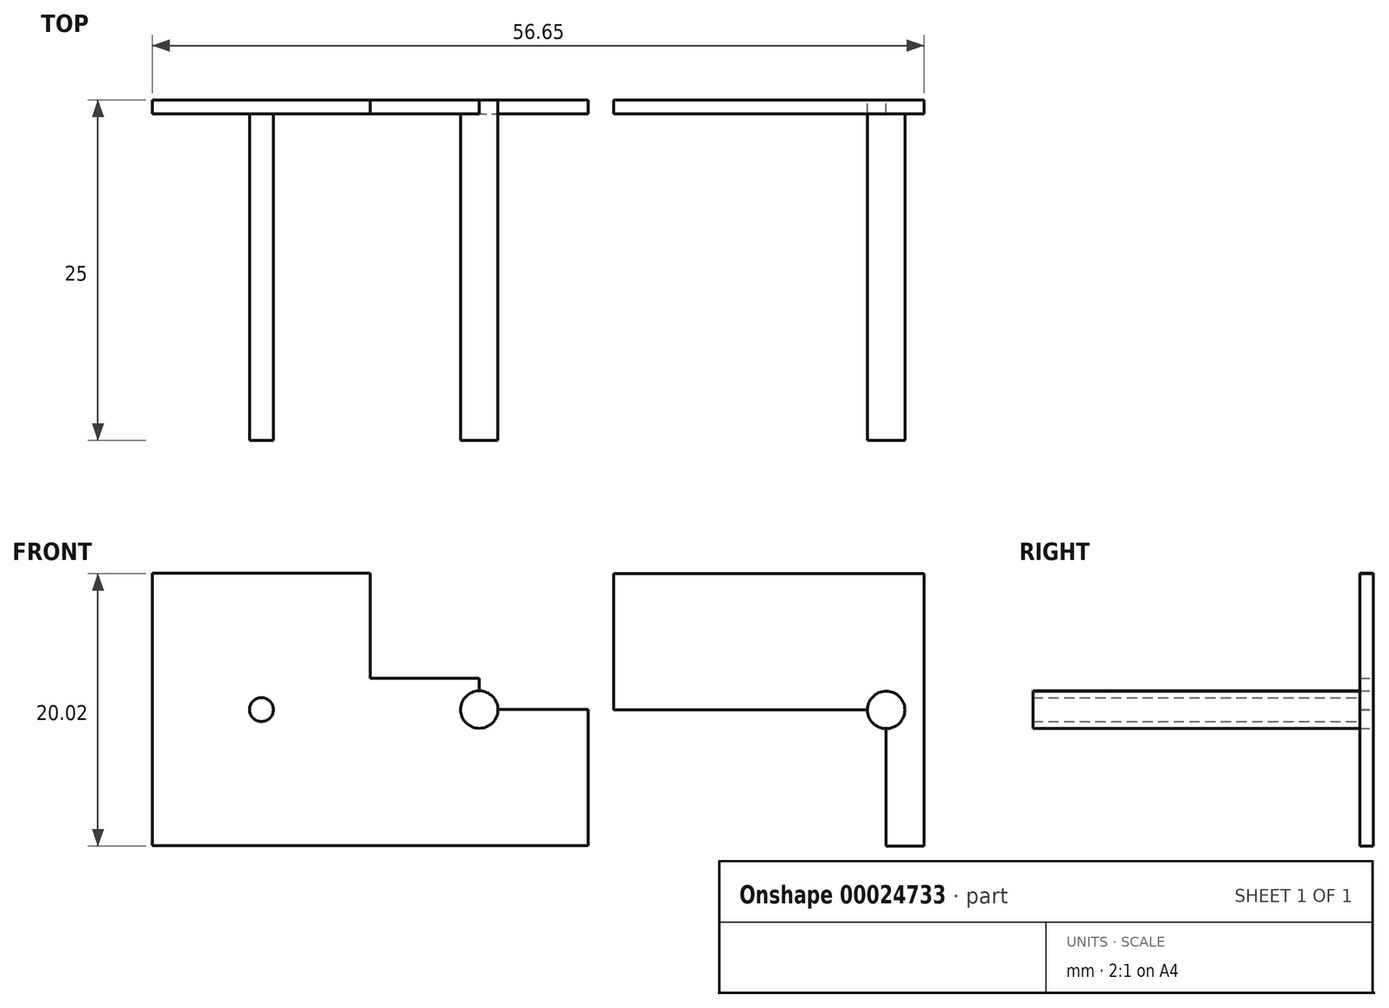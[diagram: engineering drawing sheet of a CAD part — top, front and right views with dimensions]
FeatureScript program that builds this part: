
annotation { "Feature Type Name" : "Feature", "Feature Type Description" : "" }
export const myFeature = defineFeature(function(context is Context, id is Id, definition is map)
    precondition{}
    {
        {
            var Q0;
            Q0=qCreatedBy(makeId("Front.planeOp"),FACE);
            var sketch = newSketch(context, id + "F0", { "sketchPlane" : qUnion([Q0])});
            skLineSegment(sketch, "E0.bottom", {"start": v(-17.4, 17.78) * mm, "end": v(14.6, 17.78) * mm});
            skLineSegment(sketch, "E0.top", {"start": v(-17.4, -2.22) * mm, "end": v(14.6, -2.22) * mm});
            skLineSegment(sketch, "E0.left", {"start": v(-17.4, 17.78) * mm, "end": v(-17.4, -2.22) * mm});
            skLineSegment(sketch, "E0.right", {"start": v(14.6, 17.78) * mm, "end": v(14.6, -2.22) * mm});
            skLineSegment(sketch, "E1", {"start": v(-17.4, 7.78) * mm, "end": v(14.6, 7.78) * mm});
            skLineSegment(sketch, "E2", {"start": v(-1.4, 17.78) * mm, "end": v(-1.4, -2.22) * mm});
            skLineSegment(sketch, "E3.bottom", {"start": v(-1.4, 7.78) * mm, "end": v(-9.4, 7.78) * mm});
            skLineSegment(sketch, "E3.top", {"start": v(-1.4, 11.37) * mm, "end": v(-9.4, 11.37) * mm});
            skLineSegment(sketch, "E3.left", {"start": v(-1.4, 7.78) * mm, "end": v(-1.4, 11.37) * mm});
            skLineSegment(sketch, "E3.right", {"start": v(-9.4, 7.78) * mm, "end": v(-9.4, 11.37) * mm});
            skLineSegment(sketch, "E4.bottom", {"start": v(-1.4, 7.78) * mm, "end": v(6.6, 7.78) * mm});
            skLineSegment(sketch, "E4.top", {"start": v(-1.4, 10.08) * mm, "end": v(6.6, 10.08) * mm});
            skLineSegment(sketch, "E4.left", {"start": v(-1.4, 7.78) * mm, "end": v(-1.4, 10.08) * mm});
            skLineSegment(sketch, "E4.right", {"start": v(6.6, 7.78) * mm, "end": v(6.6, 10.08) * mm});
            skCircle(sketch, "E5", {"center": v(-9.4, 7.78) * mm, "radius": 0.87 * mm});
            skCircle(sketch, "E6", {"center": v(6.6, 7.78) * mm, "radius": 1.38 * mm});
            skSolve(sketch);
        }
        {
            var Q0;
            {var subQ5=sQuery(id+"F0.wireOp",EDGE,"E3.top");Q0=makeQuery(id+"F0.imprint","IMPRINT",FACE,{"disambiguationData":[TD([[makeQuery(id+"F0.imprint","IMPRINT",EDGE,{"derivedFrom":subQ5}),-1.0]])]});}
            var Q1;
            {var subQ7=sQuery(id+"F0.wireOp",EDGE,"E0.top");var subQ9=sQuery(id+"F0.wireOp",EDGE,"E0.left");var subQ11=makeQuery(id+"F0.imprint","INTERSECT",VERTEX,{"derivedFrom":[subQ7,subQ9]});Q1=makeQuery(id+"F0.imprint","IMPRINT",FACE,{"disambiguationData":[TD([[makeQuery(id+"F0.imprint","IMPRINT",EDGE,{"disambiguationData":[TD([[subQ11,-1.0]])],"derivedFrom":subQ7}),1.0]])]});}
            var Q2;
            {var subQ6=sQuery(id+"F0.wireOp",EDGE,"E3.top");Q2=makeQuery(id+"F0.imprint","IMPRINT",FACE,{"disambiguationData":[TD([[makeQuery(id+"F0.imprint","IMPRINT",EDGE,{"derivedFrom":subQ6}),1.0]])]});}
            var Q3;
            {var subQ7=sQuery(id+"F0.wireOp",EDGE,"E0.top");var subQ9=sQuery(id+"F0.wireOp",EDGE,"E0.right");var subQ11=makeQuery(id+"F0.imprint","INTERSECT",VERTEX,{"derivedFrom":[subQ7,subQ9]});Q3=makeQuery(id+"F0.imprint","IMPRINT",FACE,{"disambiguationData":[TD([[makeQuery(id+"F0.imprint","IMPRINT",EDGE,{"disambiguationData":[TD([[subQ11,1.0]])],"derivedFrom":subQ7}),1.0]])]});}
            var Q4;
            {var subQ6=sQuery(id+"F0.wireOp",EDGE,"E3.left");Q4=makeQuery(id+"F0.imprint","IMPRINT",FACE,{"disambiguationData":[TD([[makeQuery(id+"F0.imprint","IMPRINT",EDGE,{"derivedFrom":subQ6}),-1.0]])]});}
            var Q5;
            {var subQ5=sQuery(id+"F0.wireOp",EDGE,"E4.top");Q5=makeQuery(id+"F0.imprint","IMPRINT",FACE,{"disambiguationData":[TD([[makeQuery(id+"F0.imprint","IMPRINT",EDGE,{"derivedFrom":subQ5}),-1.0]])]});}
            extrude(context, id + "F1", {"entities" : qUnion([Q0, Q1, Q2, Q3, Q4, Q5]), "depth" : 1 * mm});
        }
        {
            var Q0;
            {var subQ0=sQuery(id+"F0.wireOp",EDGE,"E5");var subQ3=sQuery(id+"F0.wireOp",EDGE,"E1");var subQ4=makeQuery(id+"F0.imprint","INTERSECT",VERTEX,{"derivedFrom":[subQ3,subQ0]});Q0=makeQuery(id+"F0.imprint","IMPRINT",FACE,{"disambiguationData":[TD([[makeQuery(id+"F0.imprint","IMPRINT",EDGE,{"disambiguationData":[TD([[subQ4,-1.0]])],"derivedFrom":subQ0}),1.0]])]});}
            var Q1;
            {var subQ0=sQuery(id+"F0.wireOp",EDGE,"E5");var subQ3=sQuery(id+"F0.wireOp",EDGE,"E1");var subQ4=makeQuery(id+"F0.imprint","INTERSECT",VERTEX,{"derivedFrom":[subQ3,subQ0]});Q1=makeQuery(id+"F0.imprint","IMPRINT",FACE,{"disambiguationData":[TD([[makeQuery(id+"F0.imprint","IMPRINT",EDGE,{"disambiguationData":[TD([[subQ4,1.0]])],"derivedFrom":subQ0}),1.0]])]});}
            var Q2;
            {var subQ0=sQuery(id+"F0.wireOp",EDGE,"E5");var subQ3=sQuery(id+"F0.wireOp",EDGE,"E3.bottom");var subQ4=makeQuery(id+"F0.imprint","INTERSECT",VERTEX,{"derivedFrom":[subQ3,subQ0]});Q2=makeQuery(id+"F0.imprint","IMPRINT",FACE,{"disambiguationData":[TD([[makeQuery(id+"F0.imprint","IMPRINT",EDGE,{"disambiguationData":[TD([[subQ4,-1.0]])],"derivedFrom":subQ0}),1.0]])]});}
            extrude(context, id + "F2", {"entities" : qUnion([Q0, Q1, Q2]), "operationType" : NewBodyOperationType.ADD, "depth" : 25 * mm});
        }
        {
            var Q0;
            {var subQ0=sQuery(id+"F0.wireOp",EDGE,"E6");var subQ3=sQuery(id+"F0.wireOp",EDGE,"E1");var subQ4=makeQuery(id+"F0.imprint","INTERSECT",VERTEX,{"derivedFrom":[subQ3,subQ0]});Q0=makeQuery(id+"F0.imprint","IMPRINT",FACE,{"disambiguationData":[TD([[makeQuery(id+"F0.imprint","IMPRINT",EDGE,{"disambiguationData":[TD([[subQ4,1.0]])],"derivedFrom":subQ0}),1.0]])]});}
            var Q1;
            {var subQ0=sQuery(id+"F0.wireOp",EDGE,"E6");var subQ3=sQuery(id+"F0.wireOp",EDGE,"E4.bottom");var subQ4=makeQuery(id+"F0.imprint","INTERSECT",VERTEX,{"derivedFrom":[subQ3,subQ0]});Q1=makeQuery(id+"F0.imprint","IMPRINT",FACE,{"disambiguationData":[TD([[makeQuery(id+"F0.imprint","IMPRINT",EDGE,{"disambiguationData":[TD([[subQ4,1.0]])],"derivedFrom":subQ0}),1.0]])]});}
            var Q2;
            {var subQ0=sQuery(id+"F0.wireOp",EDGE,"E6");var subQ3=sQuery(id+"F0.wireOp",EDGE,"E1");var subQ4=makeQuery(id+"F0.imprint","INTERSECT",VERTEX,{"derivedFrom":[subQ3,subQ0]});Q2=makeQuery(id+"F0.imprint","IMPRINT",FACE,{"disambiguationData":[TD([[makeQuery(id+"F0.imprint","IMPRINT",EDGE,{"disambiguationData":[TD([[subQ4,-1.0]])],"derivedFrom":subQ0}),1.0]])]});}
            extrude(context, id + "F3", {"entities" : qUnion([Q0, Q1, Q2]), "operationType" : NewBodyOperationType.ADD, "depth" : 25 * mm});
        }
        {
            var Q0;
            Q0=qCreatedBy(makeId("Front.planeOp"),FACE);
            var sketch = newSketch(context, id + "F4", { "sketchPlane" : qUnion([Q0])});
            skLineSegment(sketch, "E7.bottom", {"start": v(16.48, 17.76) * mm, "end": v(39.25, 17.76) * mm});
            skLineSegment(sketch, "E7.top", {"start": v(16.48, -2.24) * mm, "end": v(39.25, -2.24) * mm});
            skLineSegment(sketch, "E7.left", {"start": v(16.48, 17.76) * mm, "end": v(16.48, -2.24) * mm});
            skLineSegment(sketch, "E7.right", {"start": v(39.25, 17.76) * mm, "end": v(39.25, -2.24) * mm});
            skLineSegment(sketch, "E8.bottom", {"start": v(16.48, -2.24) * mm, "end": v(36.48, -2.24) * mm});
            skLineSegment(sketch, "E8.top", {"start": v(16.48, 7.76) * mm, "end": v(36.48, 7.76) * mm});
            skLineSegment(sketch, "E8.left", {"start": v(16.48, -2.24) * mm, "end": v(16.48, 7.76) * mm});
            skLineSegment(sketch, "E8.right", {"start": v(36.48, -2.24) * mm, "end": v(36.48, 7.76) * mm});
            skCircle(sketch, "E9", {"center": v(36.48, 7.76) * mm, "radius": 1.38 * mm});
            skSolve(sketch);
        }
        {
            var Q0;
            Q0=makeQuery(id+"F4.imprint","IMPRINT",FACE,{"disambiguationData":[TD([[makeQuery(id+"F4.imprint","IMPRINT",EDGE,{"derivedFrom":sQuery(id+"F4.wireOp",EDGE,"E7.bottom")}),-1.0]])]});
            var Q1;
            {var subQ5=sQuery(id+"F4.wireOp",EDGE,"E8.bottom");Q1=makeQuery(id+"F4.imprint","IMPRINT",FACE,{"disambiguationData":[TD([[makeQuery(id+"F4.imprint","IMPRINT",EDGE,{"derivedFrom":subQ5}),1.0]])]});}
            extrude(context, id + "F5", {"entities" : qUnion([Q0, Q1]), "depth" : 1 * mm});
        }
        {
            var Q0;
            {var subQ1=sQuery(id+"F4.wireOp",EDGE,"E8.right");var subQ3=sQuery(id+"F4.wireOp",EDGE,"E8.top");var subQ5=makeQuery(id+"F4.imprint","INTERSECT",VERTEX,{"derivedFrom":[subQ3,subQ1]});Q0=makeQuery(id+"F4.imprint","IMPRINT",FACE,{"disambiguationData":[TD([[makeQuery(id+"F4.imprint","IMPRINT",EDGE,{"disambiguationData":[TD([[subQ5,1.0]])],"derivedFrom":subQ3}),-1.0]])]});}
            var Q1;
            {var subQ1=sQuery(id+"F4.wireOp",EDGE,"E8.right");var subQ3=sQuery(id+"F4.wireOp",EDGE,"E8.top");var subQ5=makeQuery(id+"F4.imprint","INTERSECT",VERTEX,{"derivedFrom":[subQ3,subQ1]});Q1=makeQuery(id+"F4.imprint","IMPRINT",FACE,{"disambiguationData":[TD([[makeQuery(id+"F4.imprint","IMPRINT",EDGE,{"disambiguationData":[TD([[subQ5,1.0]])],"derivedFrom":subQ3}),1.0]])]});}
            extrude(context, id + "F6", {"entities" : qUnion([Q0, Q1]), "operationType" : NewBodyOperationType.ADD, "depth" : 25 * mm});
        }
    });
